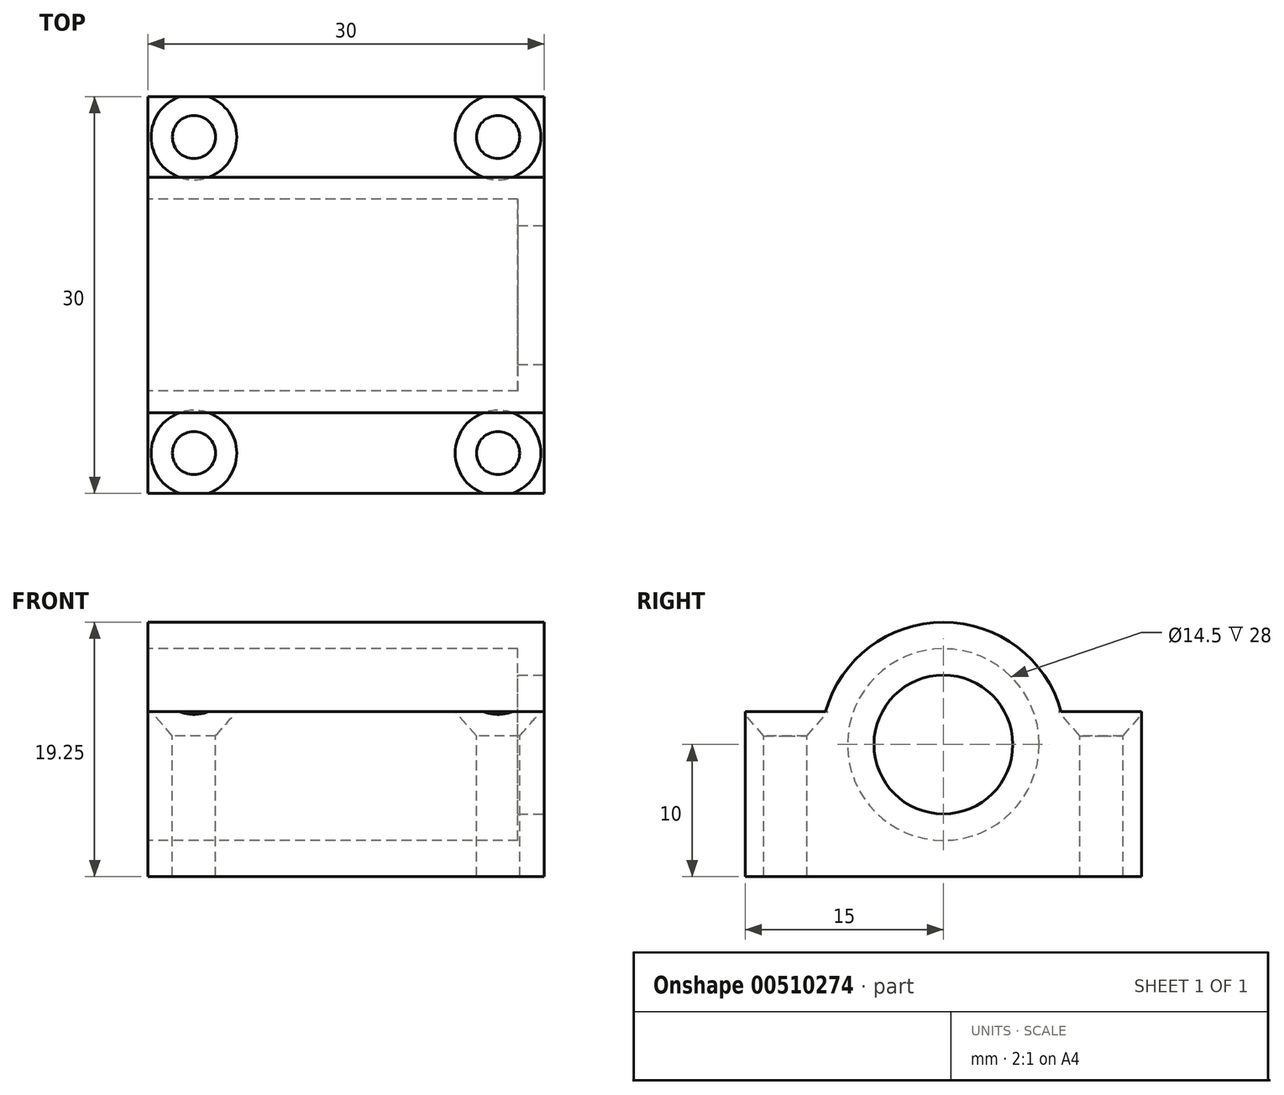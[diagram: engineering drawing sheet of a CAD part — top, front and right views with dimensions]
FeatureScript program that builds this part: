
annotation { "Feature Type Name" : "Feature", "Feature Type Description" : "" }
export const myFeature = defineFeature(function(context is Context, id is Id, definition is map)
    precondition{}
    {
        {
            var Q0;
            Q0=qCreatedBy(makeId("Right.planeOp"),FACE);
            var sketch = newSketch(context, id + "F0", { "sketchPlane" : qUnion([Q0])});
            skLineSegment(sketch, "E0.top", {"start": v(15, -10) * mm, "end": v(-15, -10) * mm});
            skLineSegment(sketch, "E0.left", {"start": v(15, 2.5) * mm, "end": v(15, -10) * mm});
            skLineSegment(sketch, "E0.right", {"start": v(-15, 2.5) * mm, "end": v(-15, -10) * mm});
            skPoint(sketch, "E0.middle", {"position": v(0, 0) * mm});
            skCircle(sketch, "E1", {"center": v(0, 0) * mm, "radius": 7.25 * mm});
            skLineSegment(sketch, "E2", {"start": v(15, 0) * mm, "end": v(7.25, 0) * mm});
            skLineSegment(sketch, "E3", {"start": v(-15, 0) * mm, "end": v(-7.25, 0) * mm});
            skLineSegment(sketch, "E4", {"start": v(-15, 2.5) * mm, "end": v(-8.9, 2.5) * mm});
            skLineSegment(sketch, "E5", {"start": v(0, 0) * mm, "end": v(0, 20.89) * mm, "construction": true});
            skLineSegment(sketch, "E6.MirrorCS", {"start": v(15, 2.5) * mm, "end": v(8.9, 2.5) * mm});
            skArc(sketch, "E7.trimOffspring", {"start": v(8.9, 2.5) * mm, "mid": v(0, 9.25) * mm, "end": v(-8.9, 2.5) * mm});
            skLineSegment(sketch, "E8", {"start": v(0, 0) * mm, "end": v(0, -10) * mm, "construction": true});
            skLineSegment(sketch, "E9", {"start": v(-7.25, 0) * mm, "end": v(7.25, 0) * mm, "construction": true});
            skSolve(sketch);
        }
        {
            var Q0;
            {var subQ4=sQuery(id+"F0.wireOp",EDGE,"E0.top");Q0=makeQuery(id+"F0.imprint","IMPRINT",FACE,{"disambiguationData":[TD([[makeQuery(id+"F0.imprint","IMPRINT",EDGE,{"derivedFrom":subQ4}),-1.0]])]});}
            extrude(context, id + "F1", {"entities" : qUnion([Q0]), "endBound" : BoundingType.SYMMETRIC, "depth" : 30 * mm, "offsetDistance" : 25 * mm});
        }
        {
            var Q0;
            {var subQ0=sQuery(id+"F0.wireOp",EDGE,"E2");Q0=makeQuery(id+"F0.imprint","IMPRINT",FACE,{"disambiguationData":[TD([[makeQuery(id+"F0.imprint","IMPRINT",EDGE,{"derivedFrom":subQ0}),-1.0]])]});}
            extrude(context, id + "F2", {"entities" : qUnion([Q0]), "endBound" : BoundingType.SYMMETRIC, "depth" : 30 * mm, "offsetDistance" : 25 * mm});
        }
        {
            var Q0;
            Q0=makeQuery(id+"F1.opExtrude","CAP_FACE",FACE,{"disambiguationData":[OSD([sQuery(id+"F0.wireOp",EDGE,"E0.top"),sQuery(id+"F0.wireOp",EDGE,"E0.left"),sQuery(id+"F0.wireOp",EDGE,"E0.right"),sQuery(id+"F0.wireOp",EDGE,"E1"),sQuery(id+"F0.wireOp",EDGE,"E2"),sQuery(id+"F0.wireOp",EDGE,"E3")])],"isStart":false});
            var sketch = newSketch(context, id + "F3", { "sketchPlane" : qUnion([Q0])});
            skCircle(sketch, "E10.0", {"center": v(0, 0) * mm, "radius": 7.25 * mm});
            skCircle(sketch, "E11.0", {"center": v(0, 0) * mm, "radius": 5.25 * mm});
            skLineSegment(sketch, "E12", {"start": v(-7.25, 0) * mm, "end": v(-5.25, 0) * mm});
            skLineSegment(sketch, "E13.MirrorCS", {"start": v(7.25, 0) * mm, "end": v(5.25, 0) * mm});
            skSolve(sketch);
        }
        {
            var Q0;
            {var subQ2=sQuery(id+"F3.wireOp",EDGE,"E12");Q0=makeQuery(id+"F3.imprint","IMPRINT",FACE,{"disambiguationData":[TD([[makeQuery(id+"F3.imprint","IMPRINT",EDGE,{"derivedFrom":subQ2}),1.0]])]});}
            extrude(context, id + "F4", {"entities" : qUnion([Q0]), "operationType" : NewBodyOperationType.ADD, "oppositeDirection" : true, "depth" : 2 * mm, "offsetDistance" : 25 * mm});
        }
        {
            var Q0;
            {var subQ2=sQuery(id+"F3.wireOp",EDGE,"E12");Q0=makeQuery(id+"F3.imprint","IMPRINT",FACE,{"disambiguationData":[TD([[makeQuery(id+"F3.imprint","IMPRINT",EDGE,{"derivedFrom":subQ2}),-1.0]])]});}
            extrude(context, id + "F5", {"entities" : qUnion([Q0]), "operationType" : NewBodyOperationType.ADD, "oppositeDirection" : true, "depth" : 2 * mm, "offsetDistance" : 25 * mm});
        }
        {
            var Q0;
            Q0=makeQuery(id+"F2.opExtrude","SWEPT_FACE",FACE,{"disambiguationData":[OSD([sQuery(id+"F0.wireOp",EDGE,"E6.MirrorCS")])]});
            var sketch = newSketch(context, id + "F6", { "sketchPlane" : qUnion([Q0])});
            skLineSegment(sketch, "E14", {"start": v(-15, 11.95) * mm, "end": v(15, 11.95) * mm, "construction": true});
            skLineSegment(sketch, "E15", {"start": v(0, 0) * mm, "end": v(14.83, 0) * mm, "construction": true});
            skLineSegment(sketch, "E16", {"start": v(11.5, 15) * mm, "end": v(11.5, 0) * mm, "construction": true});
            skLineSegment(sketch, "E17", {"start": v(0, 0) * mm, "end": v(0, 15) * mm, "construction": true});
            skPoint(sketch, "E18", {"position": v(11.5, 11.95) * mm});
            skPoint(sketch, "E19.MirrorP", {"position": v(-11.5, 11.95) * mm});
            skPoint(sketch, "E20.MirrorP", {"position": v(11.5, -11.95) * mm});
            skPoint(sketch, "E21.MirrorP", {"position": v(-11.5, -11.95) * mm});
            skSolve(sketch);
        }
        {
            var Q0;
            Q0=sQuery(id+"F6.wireOp",VERTEX,"E19.MirrorP");
            var Q1;
            Q1=sQuery(id+"F6.wireOp",VERTEX,"E18");
            var Q2;
            Q2=sQuery(id+"F6.wireOp",VERTEX,"E20.MirrorP");
            var Q3;
            Q3=sQuery(id+"F6.wireOp",VERTEX,"E21.MirrorP");
            var Q4;
            Q4=makeQuery(id+"F2.opExtrude","SWEPT_BODY",BODY,{"disambiguationData":[OSD([sQuery(id+"F0.wireOp",EDGE,"E0.left"),sQuery(id+"F0.wireOp",EDGE,"E0.right"),sQuery(id+"F0.wireOp",EDGE,"E1"),sQuery(id+"F0.wireOp",EDGE,"E2"),sQuery(id+"F0.wireOp",EDGE,"E3"),sQuery(id+"F0.wireOp",EDGE,"E4"),sQuery(id+"F0.wireOp",EDGE,"E6.MirrorCS"),sQuery(id+"F0.wireOp",EDGE,"E7.trimOffspring")])]});
            var Q5;
            Q5=makeQuery(id+"F1.opExtrude","SWEPT_BODY",BODY,{"disambiguationData":[OSD([sQuery(id+"F0.wireOp",EDGE,"E0.top"),sQuery(id+"F0.wireOp",EDGE,"E0.left"),sQuery(id+"F0.wireOp",EDGE,"E0.right"),sQuery(id+"F0.wireOp",EDGE,"E1"),sQuery(id+"F0.wireOp",EDGE,"E2"),sQuery(id+"F0.wireOp",EDGE,"E3")])]});
            hole(context, id + "F7", {"style" : HoleStyle.C_SINK, "endStyle" : HoleEndStyle.THROUGH, "standardTappedOrClearance" : lookupTablePath({ "standard" : "ANSI", "fit" : "Normal (ASME)", "size" : "#4", "type" : "Clearance" }), "standardBlindInLast" : lookupTablePath({ "fit" : "Free", "standard" : "ANSI", "size" : "#4", "type" : "Clearance" }), "holeDiameter" : 3.26 * mm, "cSinkDiameter" : 6.48 * mm, "cSinkAngle" : 82 * degree, "isTappedThrough" : true, "tappedDepth" : 12 * mm, "tapClearance" : 3, "locations" : qUnion([Q0, Q1, Q2, Q3]), "scope" : qUnion([Q4, Q5])});
        }
    });
